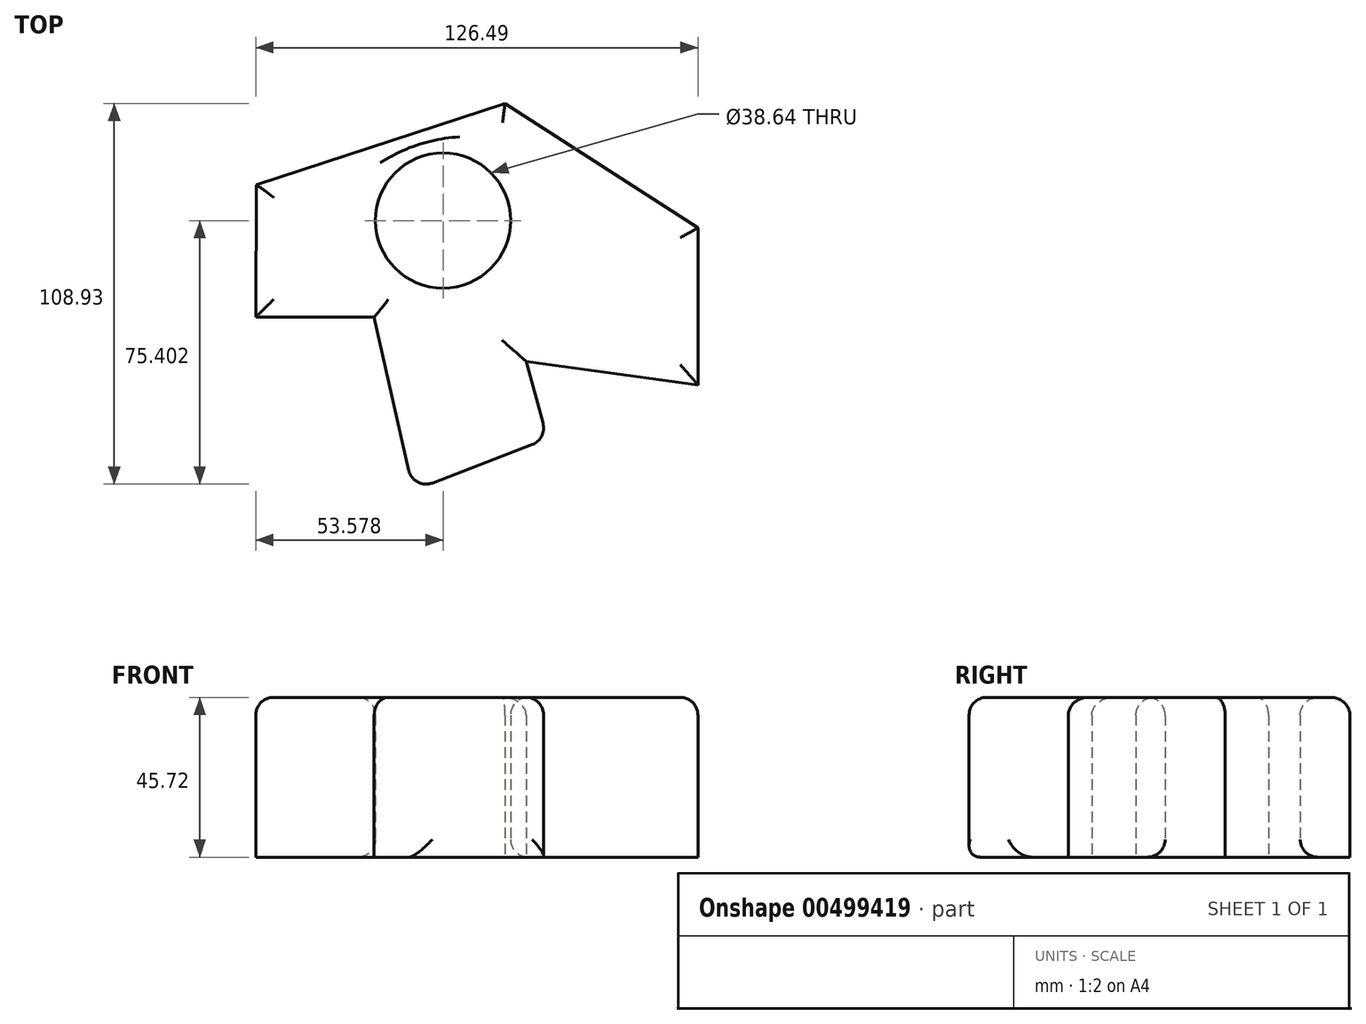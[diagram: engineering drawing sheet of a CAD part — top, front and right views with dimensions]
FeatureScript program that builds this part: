
annotation { "Feature Type Name" : "Feature", "Feature Type Description" : "" }
export const myFeature = defineFeature(function(context is Context, id is Id, definition is map)
    precondition{}
    {
        {
            var Q0;
            Q0=qCreatedBy(makeId("Top.planeOp"),FACE);
            var sketch = newSketch(context, id + "F0", { "sketchPlane" : qUnion([Q0])});
            skLineSegment(sketch, "E0", {"start": v(-58.01, 30.7) * mm, "end": v(13.13, 53.93) * mm});
            skLineSegment(sketch, "E1", {"start": v(13.13, 53.93) * mm, "end": v(68.3, 18.27) * mm});
            skLineSegment(sketch, "E2", {"start": v(68.3, 18.27) * mm, "end": v(68.3, -26.61) * mm});
            skLineSegment(sketch, "E3", {"start": v(68.3, -26.61) * mm, "end": v(19.16, -19.87) * mm});
            skLineSegment(sketch, "E4", {"start": v(19.16, -19.87) * mm, "end": v(25.2, -42.05) * mm});
            skLineSegment(sketch, "E5", {"start": v(25.2, -42.05) * mm, "end": v(-13.13, -56.77) * mm});
            skLineSegment(sketch, "E6", {"start": v(-13.13, -56.77) * mm, "end": v(-24.3, -7.27) * mm});
            skLineSegment(sketch, "E7", {"start": v(-24.3, -7.27) * mm, "end": v(-58.19, -7.27) * mm});
            skLineSegment(sketch, "E8", {"start": v(-58.19, -7.27) * mm, "end": v(-58.01, 30.7) * mm});
            skCircle(sketch, "E9", {"center": v(-4.61, 20.4) * mm, "radius": 19.32 * mm});
            skSolve(sketch);
        }
        {
            var Q0;
            Q0=makeQuery(id+"F0.imprint","IMPRINT",FACE,{"disambiguationData":[TD([[makeQuery(id+"F0.imprint","IMPRINT",EDGE,{"derivedFrom":sQuery(id+"F0.wireOp",EDGE,"E0")}),-1.0]])]});
            extrude(context, id + "F1", {"entities" : qUnion([Q0]), "depth" : 45.72 * mm});
        }
        {
            var Q0;
            Q0=makeQuery(id+"F1.opExtrude","SWEPT_FACE",FACE,{"disambiguationData":[OSD([sQuery(id+"F0.wireOp",EDGE,"E5")])]});
            var Q1;
            Q1=makeQuery(id+"F1.opExtrude","SWEPT_FACE",FACE,{"disambiguationData":[OSD([sQuery(id+"F0.wireOp",EDGE,"E9")])]});
            var Q2;
            Q2=makeQuery(id+"F1.opExtrude","CAP_EDGE",EDGE,{"disambiguationData":[OSD([sQuery(id+"F0.wireOp",EDGE,"E9")])],"isStart":false});
            var Q3;
            Q3=makeQuery(id+"F1.opExtrude","CAP_FACE",FACE,{"disambiguationData":[OSD([sQuery(id+"F0.wireOp",EDGE,"E0"),sQuery(id+"F0.wireOp",EDGE,"E1"),sQuery(id+"F0.wireOp",EDGE,"E2"),sQuery(id+"F0.wireOp",EDGE,"E3"),sQuery(id+"F0.wireOp",EDGE,"E4"),sQuery(id+"F0.wireOp",EDGE,"E5"),sQuery(id+"F0.wireOp",EDGE,"E6"),sQuery(id+"F0.wireOp",EDGE,"E7"),sQuery(id+"F0.wireOp",EDGE,"E8"),sQuery(id+"F0.wireOp",EDGE,"E9")])],"isStart":false});
            fillet(context, id + "F2", {"entities" : qUnion([Q0, Q1, Q2, Q3]), "radius" : 5.08 * mm, "tangentPropagation" : true, "allowEdgeOverflow" : false});
        }
    });
